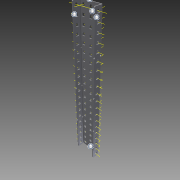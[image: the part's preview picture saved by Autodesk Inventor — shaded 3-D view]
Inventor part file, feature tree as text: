
AUTODESK INVENTOR PART (.ipt)
format: ipt  version: 2015 SP1 (Build 190203100, 203)  size: 2,133,504 bytes
history: native  units: in
note: dims shown in document units (in); Inventor stores cm internally (conversion verified against a paired STEP export)
features: other x106, pattern_linear x2, sheet_metal_op x1, extrude x1, imported_body x1, sketch x1
ambient origin geometry x8: Origin, YZ Plane, XZ Plane, XY Plane, X Axis, Y Axis, Z Axis, Center Point
bodies: Body1 (feature_tree)
feature tree (112):
  sheet_metal_op  "Fold1"
  other  "C-Channel"
  extrude  "length cut"  Depth=1.1811in
  other  "Work Point1"
  other  "Work Point2"
  other  "Work Point3"
  other  "top axis"
  other  "front axis"
  other  "back axis"
  pattern_linear  "top axes"  Count1=20  [1 undecoded]
  pattern_linear  "horiz axes"  Spacing1=0.5in  [1 undecoded]
  other  "Left Plane"
  other  "Right Plane"
  imported_body  "Base1"
  sketch  "Sketch1"  dims[d1=0.0in d2=1.1811in d4=0.5in d5=7.874in d7=0.5in d8=7.874in d10=0.5in d12=-10.0in d17=0.0in d18=0.0in d19=0.0in d20=0.0in d21=0.0in]
  other  "Work Axis4"
  other  "Work Axis5"
  other  "Work Axis6"
  other  "Work Axis7"
  other  "Work Axis8"
  other  "Work Axis9"
  other  "Work Axis10"
  other  "Work Axis11"
  other  "Work Axis12"
  other  "Work Axis13"
  other  "Work Axis14"
  other  "Work Axis15"
  other  "Work Axis16"
  other  "Work Axis17"
  other  "Work Axis18"
  other  "Work Axis19"
  other  "Work Axis20"
  other  "Work Axis21"
  other  "Work Axis22"
  other  "Work Axis23"
  other  "Work Axis24"
  other  "Work Axis25"
  other  "Work Axis26"
  other  "Work Axis27"
  other  "Work Axis28"
  other  "Work Axis29"
  other  "Work Axis30"
  other  "Work Axis31"
  other  "Work Axis32"
  other  "Work Axis33"
  other  "Work Axis34"
  other  "Work Axis35"
  other  "Work Axis36"
  other  "Work Axis37"
  other  "Work Axis38"
  other  "Work Axis39"
  other  "Work Axis40"
  other  "Work Axis41"
  other  "Work Axis42"
  other  "Work Axis43"
  other  "Work Axis44"
  other  "Work Axis45"
  other  "Work Axis46"
  other  "Work Axis47"
  other  "Work Axis48"
  other  "Work Axis49"
  other  "Work Axis50"
  other  "Work Axis51"
  other  "Work Axis52"
  other  "Work Axis53"
  other  "Work Axis54"
  other  "Work Axis55"
  other  "Work Axis56"
  other  "Work Axis57"
  other  "Work Axis58"
  other  "Work Axis59"
  other  "Work Axis60"
  other  "Work Axis61"
  other  "Work Axis62"
  other  "Work Axis63"
  other  "Work Axis64"
  other  "Work Axis65"
  other  "Work Axis66"
  other  "Work Axis67"
  other  "Work Axis68"
  other  "Work Axis69"
  other  "Work Axis70"
  other  "Work Axis71"
  other  "Work Axis72"
  other  "Work Axis73"
  other  "Work Axis74"
  other  "Work Axis75"
  other  "Work Axis76"
  other  "Work Axis77"
  other  "Work Axis78"
  other  "Work Axis79"
  other  "Work Axis80"
  other  "Work Axis81"
  other  "Work Axis82"
  other  "Work Axis83"
  other  "Work Axis84"
  other  "Work Axis85"
  other  "Work Axis86"
  other  "Work Axis87"
  other  "Work Axis88"
  other  "Work Axis89"
  other  "Work Axis90"
  other  "Work Axis91"
  other  "Work Axis92"
  other  "Work Axis93"
  other  "Work Axis94"
  other  "Work Axis95"
  other  "Work Axis96"
  other  "Work Axis97"
  other  "Work Axis98"
  other  "Work Axis99"
  other  "Work Axis100"
note: 2 required parameter values undecoded (feature->parameter linkage not recoverable at this tier; creation-order binding heuristic only, values carry confidence <= 0.55)
